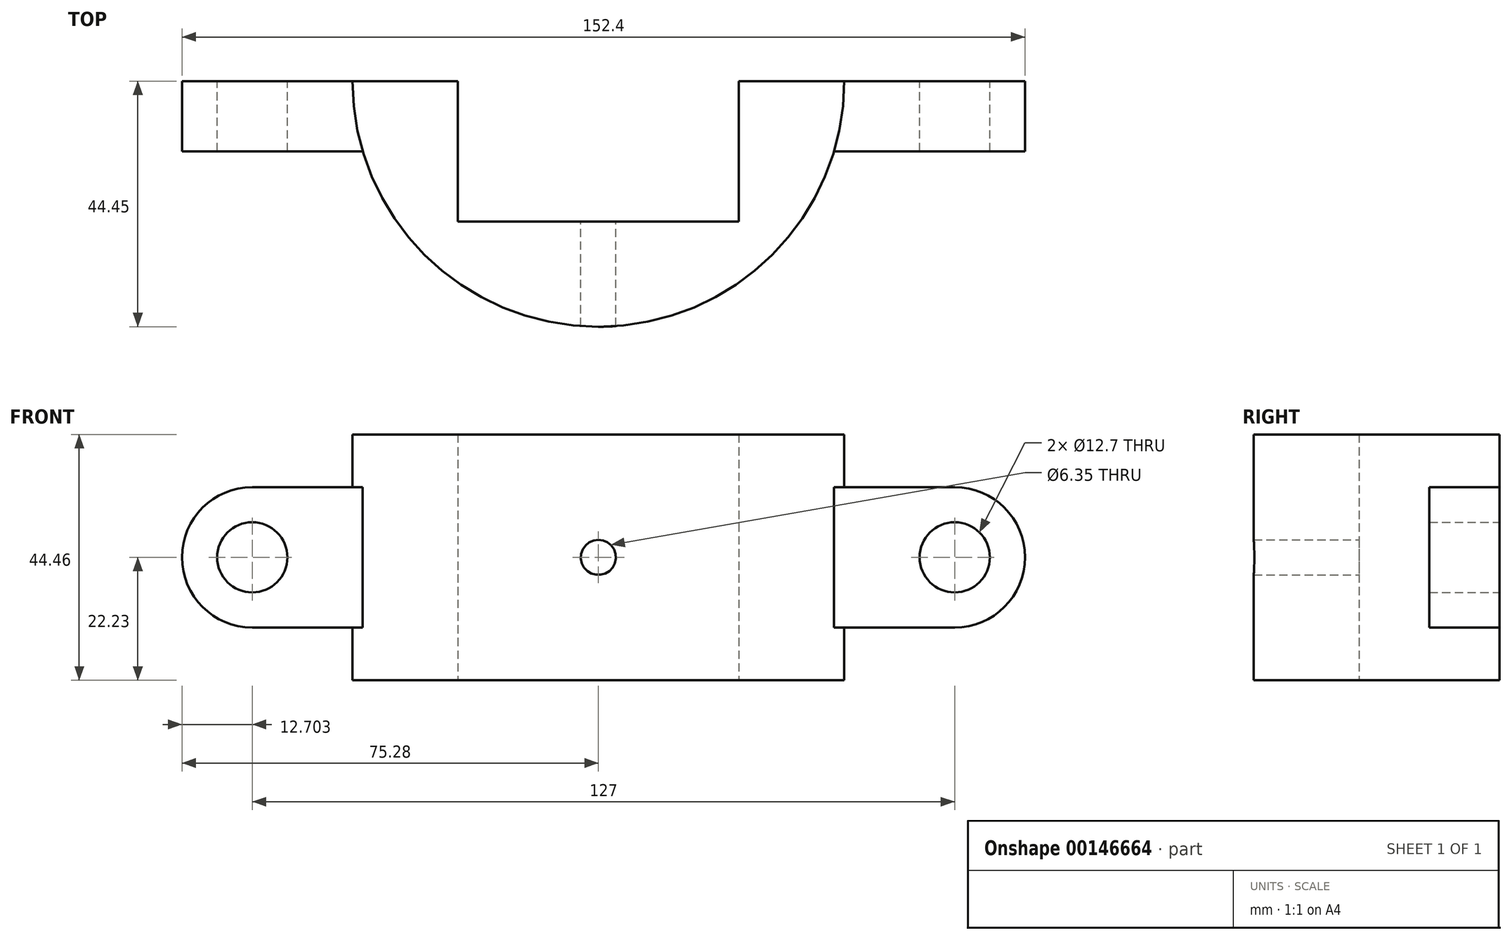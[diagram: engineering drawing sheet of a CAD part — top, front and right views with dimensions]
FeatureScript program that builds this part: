
annotation { "Feature Type Name" : "Feature", "Feature Type Description" : "" }
export const myFeature = defineFeature(function(context is Context, id is Id, definition is map)
    precondition{}
    {
        {
            var Q0;
            Q0=qCreatedBy(makeId("Front.planeOp"),FACE);
            var sketch = newSketch(context, id + "F0", { "sketchPlane" : qUnion([Q0])});
            skLineSegment(sketch, "E0", {"start": v(-62.58, 12.7) * mm, "end": v(64.42, 12.7) * mm});
            skLineSegment(sketch, "E1", {"start": v(-62.58, -12.7) * mm, "end": v(64.42, -12.7) * mm});
            skArc(sketch, "E2", {"start": v(-62.58, 12.7) * mm, "mid": v(-75.28, 0) * mm, "end": v(-62.58, -12.7) * mm});
            skArc(sketch, "E3", {"start": v(64.42, -12.7) * mm, "mid": v(77.12, 0) * mm, "end": v(64.42, 12.7) * mm});
            skCircle(sketch, "E4", {"center": v(-62.58, 0) * mm, "radius": 6.35 * mm});
            skCircle(sketch, "E5", {"center": v(64.42, 0) * mm, "radius": 6.35 * mm});
            skSolve(sketch);
        }
        {
            var Q0;
            Q0=makeQuery(id+"F0.imprint","IMPRINT",FACE,{"disambiguationData":[TD([[makeQuery(id+"F0.imprint","IMPRINT",EDGE,{"derivedFrom":sQuery(id+"F0.wireOp",EDGE,"E0")}),-1.0]])]});
            extrude(context, id + "F1", {"entities" : qUnion([Q0]), "depth" : 12.7 * mm});
        }
        {
            var Q0;
            Q0=qCreatedBy(makeId("Top.planeOp"),FACE);
            var sketch = newSketch(context, id + "F2", { "sketchPlane" : qUnion([Q0])});
            skArc(sketch, "E6", {"start": v(-44.45, 0) * mm, "mid": v(0, -44.45) * mm, "end": v(44.45, 0) * mm});
            skLineSegment(sketch, "E7", {"start": v(-44.45, 0) * mm, "end": v(44.45, 0) * mm});
            skSolve(sketch);
        }
        {
            var Q0;
            Q0=makeQuery(id+"F2.imprint","IMPRINT",FACE,{"disambiguationData":[TD([[makeQuery(id+"F2.imprint","IMPRINT",EDGE,{"derivedFrom":sQuery(id+"F2.wireOp",EDGE,"E6")}),1.0]])]});
            extrude(context, id + "F3", {"entities" : qUnion([Q0]), "operationType" : NewBodyOperationType.ADD, "endBound" : BoundingType.SYMMETRIC, "depth" : 44.45 * mm});
        }
        {
            var Q0;
            Q0=makeQuery(id+"F3.opExtrude","CAP_FACE",FACE,{"disambiguationData":[OSD([sQuery(id+"F2.wireOp",EDGE,"E6"),sQuery(id+"F2.wireOp",EDGE,"E7")])],"isStart":true});
            var sketch = newSketch(context, id + "F4", { "sketchPlane" : qUnion([Q0])});
            skLineSegment(sketch, "E8", {"start": v(-25.4, 0) * mm, "end": v(25.4, 0) * mm});
            skLineSegment(sketch, "E9", {"start": v(25.4, 0) * mm, "end": v(25.4, 25.4) * mm});
            skLineSegment(sketch, "E10", {"start": v(25.4, 25.4) * mm, "end": v(-25.4, 25.4) * mm});
            skLineSegment(sketch, "E11", {"start": v(-25.4, 25.4) * mm, "end": v(-25.4, 0) * mm});
            skSolve(sketch);
        }
        {
            var Q0;
            Q0 = qSketchRegion(id + "F4", true);
            var Q1;
            Q1=makeQuery(id+"F4.imprint","IMPRINT",FACE,{"disambiguationData":[TD([[makeQuery(id+"F4.imprint","IMPRINT",EDGE,{"derivedFrom":sQuery(id+"F4.wireOp",EDGE,"E8")}),1.0]])]});
            extrude(context, id + "F5", {"entities" : qUnion([Q0, Q1]), "operationType" : NewBodyOperationType.REMOVE, "oppositeDirection" : true, "depth" : 44.45 * mm});
        }
        {
            var Q0;
            Q0=makeQuery(id+"F5.boolean.opBoolean","COPY",FACE,{"derivedFrom":makeQuery(id+"F5.opExtrude","SWEPT_FACE",FACE,{"disambiguationData":[OSD([sQuery(id+"F4.wireOp",EDGE,"E10")])]})});
            var sketch = newSketch(context, id + "F6", { "sketchPlane" : qUnion([Q0])});
            skCircle(sketch, "E12", {"center": v(0, 0) * mm, "radius": 3.18 * mm});
            skSolve(sketch);
        }
        {
            var Q0;
            Q0 = qSketchRegion(id + "F6", true);
            extrude(context, id + "F7", {"entities" : qUnion([Q0]), "operationType" : NewBodyOperationType.REMOVE, "oppositeDirection" : true, "depth" : 25.4 * mm});
        }
    });
